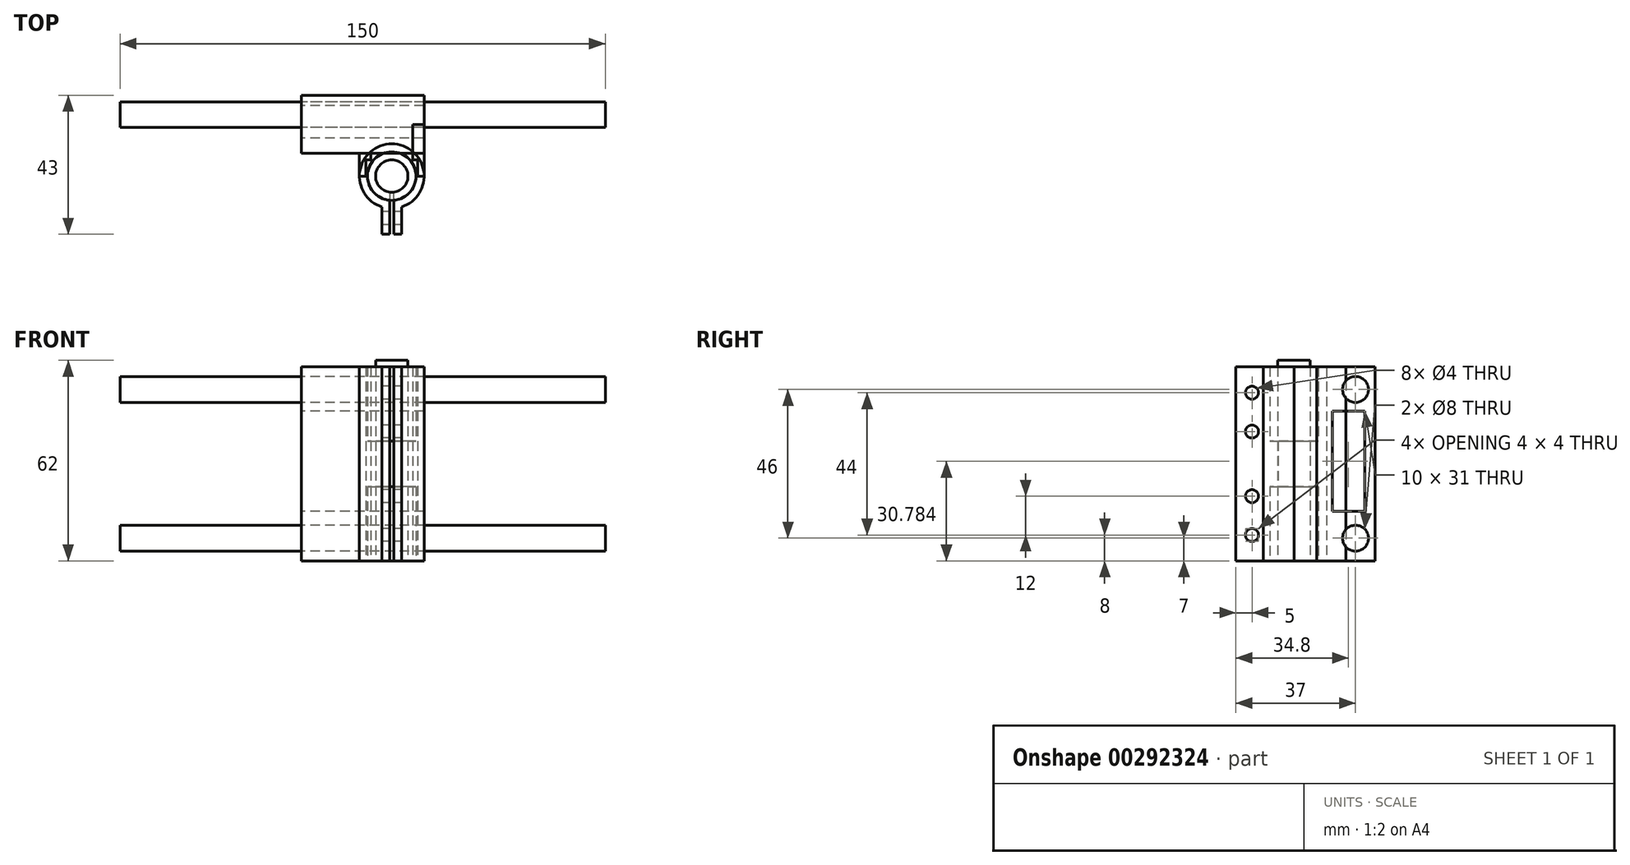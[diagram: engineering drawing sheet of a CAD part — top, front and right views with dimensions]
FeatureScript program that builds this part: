
annotation { "Feature Type Name" : "Feature", "Feature Type Description" : "" }
export const myFeature = defineFeature(function(context is Context, id is Id, definition is map)
    precondition{}
    {
        {
            var Q0;
            Q0=qCreatedBy(makeId("Top.planeOp"),FACE);
            var sketch = newSketch(context, id + "F0", { "sketchPlane" : qUnion([Q0])});
            skLineSegment(sketch, "E0.bottom", {"start": v(19, -9) * mm, "end": v(-19, -9) * mm});
            skLineSegment(sketch, "E0.top", {"start": v(19, 9) * mm, "end": v(-19, 9) * mm});
            skLineSegment(sketch, "E0.left", {"start": v(19, -9) * mm, "end": v(19, 9) * mm});
            skLineSegment(sketch, "E0.right", {"start": v(-19, -9) * mm, "end": v(-19, 9) * mm});
            skPoint(sketch, "E0.middle", {"position": v(0, 0) * mm});
            skSolve(sketch);
        }
        {
            var Q0;
            Q0=qSketchRegion(id+"F0",true);
            extrude(context, id + "F1", {"entities" : qUnion([Q0]), "depth" : 60 * mm});
        }
        {
            var Q0;
            Q0=qCreatedBy(makeId("Right.planeOp"),FACE);
            var sketch = newSketch(context, id + "F2", { "sketchPlane" : qUnion([Q0])});
            skCircle(sketch, "E1", {"center": v(0, 0) * mm, "radius": 4 * mm});
            skSolve(sketch);
        }
        {
            var Q0;
            Q0=qSketchRegion(id+"F2",true);
            extrude(context, id + "F3", {"entities" : qUnion([Q0]), "endBound" : BoundingType.SYMMETRIC, "depth" : 150 * mm});
        }
        {
            var Q0;
            Q0=makeQuery(id+"F3.opExtrude","SWEPT_BODY",BODY,{"disambiguationData":[OSD([sQuery(id+"F2.wireOp",EDGE,"E1")])]});
            transform(context, id + "F4", {"entities" : qUnion([Q0]), "transformType" : TransformType.TRANSLATION_3D, "dx" : 0 * mm, "dy" : 3 * mm, "dz" : 7 * mm, "makeCopy" : false});
        }
        {
            var Q0;
            Q0=makeQuery(id+"F3.opExtrude","SWEPT_BODY",BODY,{"disambiguationData":[OSD([sQuery(id+"F2.wireOp",EDGE,"E1")])]});
            transform(context, id + "F5", {"entities" : qUnion([Q0]), "transformType" : TransformType.COPY});
        }
        {
            var Q0;
            Q0=makeQuery(id+"F5.opPattern","COPY",BODY,{"derivedFrom":makeQuery(id+"F3.opExtrude","SWEPT_BODY",BODY,{"disambiguationData":[OSD([sQuery(id+"F2.wireOp",EDGE,"E1")])]}),"instanceName":"1"});
            transform(context, id + "F6", {"entities" : qUnion([Q0]), "transformType" : TransformType.TRANSLATION_3D, "dx" : 0 * mm, "dy" : 0 * mm, "dz" : 46 * mm, "makeCopy" : false});
        }
        {
            var Q0;
            Q0=makeQuery(id+"F3.opExtrude","SWEPT_BODY",BODY,{"disambiguationData":[OSD([sQuery(id+"F2.wireOp",EDGE,"E1")])]});
            var Q1;
            Q1=makeQuery(id+"F5.opPattern","COPY",BODY,{"derivedFrom":makeQuery(id+"F3.opExtrude","SWEPT_BODY",BODY,{"disambiguationData":[OSD([sQuery(id+"F2.wireOp",EDGE,"E1")])]}),"instanceName":"1"});
            transform(context, id + "F7", {"entities" : qUnion([Q0, Q1]), "transformType" : TransformType.COPY});
        }
        {
            var Q0;
            Q0=makeQuery(id+"F7.opPattern","COPY",BODY,{"derivedFrom":makeQuery(id+"F3.opExtrude","SWEPT_BODY",BODY,{"disambiguationData":[OSD([sQuery(id+"F2.wireOp",EDGE,"E1")])]}),"instanceName":"1"});
            var Q1;
            Q1=makeQuery(id+"F7.opPattern","COPY",BODY,{"derivedFrom":makeQuery(id+"F5.opPattern","COPY",BODY,{"derivedFrom":makeQuery(id+"F3.opExtrude","SWEPT_BODY",BODY,{"disambiguationData":[OSD([sQuery(id+"F2.wireOp",EDGE,"E1")])]}),"instanceName":"1"}),"instanceName":"1"});
            var Q2;
            Q2=makeQuery(id+"F1.opExtrude","SWEPT_BODY",BODY,{"disambiguationData":[OSD([sQuery(id+"F0.wireOp",EDGE,"E0.bottom"),sQuery(id+"F0.wireOp",EDGE,"E0.top"),sQuery(id+"F0.wireOp",EDGE,"E0.left"),sQuery(id+"F0.wireOp",EDGE,"E0.right")])]});
            booleanBodies(context, id + "F8", {"operationType" : BooleanOperationType.SUBTRACTION, "tools" : qUnion([Q0, Q1]), "targets" : qUnion([Q2])});
        }
        {
            var Q0;
            Q0=qCreatedBy(makeId("Right.planeOp"),FACE);
            var sketch = newSketch(context, id + "F9", { "sketchPlane" : qUnion([Q0])});
            skLineSegment(sketch, "E2", {"start": v(5.8, 0) * mm, "end": v(9, 0) * mm});
            skLineSegment(sketch, "E3", {"start": v(9, 0) * mm, "end": v(5.8, 0) * mm});
            skLineSegment(sketch, "E4", {"start": v(5.8, 15.28) * mm, "end": v(5.8, 46.28) * mm});
            skLineSegment(sketch, "E5", {"start": v(5.8, 15.28) * mm, "end": v(-4.2, 15.28) * mm});
            skLineSegment(sketch, "E6", {"start": v(-4.2, 15.28) * mm, "end": v(-4.2, 46.28) * mm});
            skLineSegment(sketch, "E7", {"start": v(-4.2, 46.28) * mm, "end": v(5.8, 46.28) * mm});
            skSolve(sketch);
        }
        {
            var Q0;
            Q0=qSketchRegion(id+"F9",true);
            extrude(context, id + "F10", {"entities" : qUnion([Q0]), "endBound" : BoundingType.SYMMETRIC, "depth" : 50 * mm});
        }
        {
            var Q0;
            Q0=makeQuery(id+"F10.opExtrude","SWEPT_BODY",BODY,{"disambiguationData":[OSD([sQuery(id+"F9.wireOp",EDGE,"E4"),sQuery(id+"F9.wireOp",EDGE,"E5"),sQuery(id+"F9.wireOp",EDGE,"E6"),sQuery(id+"F9.wireOp",EDGE,"E7")])]});
            var Q1;
            Q1=makeQuery(id+"F1.opExtrude","SWEPT_BODY",BODY,{"disambiguationData":[OSD([sQuery(id+"F0.wireOp",EDGE,"E0.bottom"),sQuery(id+"F0.wireOp",EDGE,"E0.top"),sQuery(id+"F0.wireOp",EDGE,"E0.left"),sQuery(id+"F0.wireOp",EDGE,"E0.right")])]});
            booleanBodies(context, id + "F11", {"operationType" : BooleanOperationType.SUBTRACTION, "tools" : qUnion([Q0]), "targets" : qUnion([Q1])});
        }
        {
            var Q0;
            Q0=qCreatedBy(makeId("Top.planeOp"),FACE);
            var sketch = newSketch(context, id + "F12", { "sketchPlane" : qUnion([Q0])});
            skCircle(sketch, "E8", {"center": v(0, 0) * mm, "radius": 7.5 * mm});
            skSolve(sketch);
        }
        {
            var Q0;
            Q0=qSketchRegion(id+"F12",true);
            extrude(context, id + "F13", {"entities" : qUnion([Q0]), "depth" : 23 * mm});
        }
        {
            var Q0;
            Q0=makeQuery(id+"F13.opExtrude","SWEPT_BODY",BODY,{"disambiguationData":[OSD([sQuery(id+"F12.wireOp",EDGE,"E8")])]});
            transform(context, id + "F14", {"entities" : qUnion([Q0]), "transformType" : TransformType.TRANSLATION_3D, "dx" : 8 * mm, "dy" : -16 * mm, "dz" : 0 * mm, "makeCopy" : false});
        }
        {
            var Q0;
            Q0=makeQuery(id+"F13.opExtrude","SWEPT_BODY",BODY,{"disambiguationData":[OSD([sQuery(id+"F12.wireOp",EDGE,"E8")])]});
            transform(context, id + "F15", {"entities" : qUnion([Q0]), "transformType" : TransformType.TRANSLATION_3D, "dx" : 0 * mm, "dy" : 2 * mm, "dz" : 0 * mm, "makeCopy" : false});
        }
        {
            var Q0;
            Q0=makeQuery(id+"F13.opExtrude","SWEPT_BODY",BODY,{"disambiguationData":[OSD([sQuery(id+"F12.wireOp",EDGE,"E8")])]});
            transform(context, id + "F16", {"entities" : qUnion([Q0]), "transformType" : TransformType.COPY});
        }
        {
            var Q0;
            Q0=makeQuery(id+"F16.opPattern","COPY",BODY,{"derivedFrom":makeQuery(id+"F13.opExtrude","SWEPT_BODY",BODY,{"disambiguationData":[OSD([sQuery(id+"F12.wireOp",EDGE,"E8")])]}),"instanceName":"1"});
            transform(context, id + "F17", {"entities" : qUnion([Q0]), "transformType" : TransformType.TRANSLATION_3D, "dx" : 0 * mm, "dy" : 0 * mm, "dz" : 37 * mm, "makeCopy" : false});
        }
        {
            var Q0;
            Q0=qCreatedBy(makeId("Top.planeOp"),FACE);
            var sketch = newSketch(context, id + "F18", { "sketchPlane" : qUnion([Q0])});
            skCircle(sketch, "E9", {"center": v(0, 0) * mm, "radius": 5 * mm});
            skSolve(sketch);
        }
        {
            var Q0;
            Q0=qSketchRegion(id+"F18",true);
            extrude(context, id + "F19", {"entities" : qUnion([Q0]), "depth" : 62 * mm});
        }
        {
            var Q0;
            Q0=makeQuery(id+"F19.opExtrude","SWEPT_BODY",BODY,{"disambiguationData":[OSD([sQuery(id+"F18.wireOp",EDGE,"E9")])]});
            transform(context, id + "F20", {"entities" : qUnion([Q0]), "transformType" : TransformType.TRANSLATION_3D, "dx" : 8 * mm, "dy" : -14 * mm, "dz" : 0 * mm, "makeCopy" : false});
        }
        {
            var Q0;
            Q0=makeQuery(id+"F13.opExtrude","SWEPT_BODY",BODY,{"disambiguationData":[OSD([sQuery(id+"F12.wireOp",EDGE,"E8")])]});
            var Q1;
            Q1=makeQuery(id+"F16.opPattern","COPY",BODY,{"derivedFrom":makeQuery(id+"F13.opExtrude","SWEPT_BODY",BODY,{"disambiguationData":[OSD([sQuery(id+"F12.wireOp",EDGE,"E8")])]}),"instanceName":"1"});
            var Q2;
            Q2=makeQuery(id+"F19.opExtrude","SWEPT_BODY",BODY,{"disambiguationData":[OSD([sQuery(id+"F18.wireOp",EDGE,"E9")])]});
            transform(context, id + "F21", {"entities" : qUnion([Q0, Q1, Q2]), "transformType" : TransformType.COPY});
        }
        {
            var Q0;
            Q0=qCreatedBy(makeId("Top.planeOp"),FACE);
            var sketch = newSketch(context, id + "F22", { "sketchPlane" : qUnion([Q0])});
            skCircle(sketch, "E10", {"center": v(0, 0) * mm, "radius": 10 * mm});
            skSolve(sketch);
        }
        {
            var Q0;
            Q0=qSketchRegion(id+"F22",true);
            extrude(context, id + "F23", {"entities" : qUnion([Q0]), "depth" : 60 * mm});
        }
        {
            var Q0;
            Q0=makeQuery(id+"F23.opExtrude","SWEPT_BODY",BODY,{"disambiguationData":[OSD([sQuery(id+"F22.wireOp",EDGE,"E10")])]});
            transform(context, id + "F24", {"entities" : qUnion([Q0]), "transformType" : TransformType.TRANSLATION_3D, "dx" : 9 * mm, "dy" : -10 * mm, "dz" : 0 * mm, "makeCopy" : false});
        }
        {
            var Q0;
            Q0=makeQuery(id+"F23.opExtrude","SWEPT_BODY",BODY,{"disambiguationData":[OSD([sQuery(id+"F22.wireOp",EDGE,"E10")])]});
            transform(context, id + "F25", {"entities" : qUnion([Q0]), "transformType" : TransformType.TRANSLATION_3D, "dx" : -1 * mm, "dy" : -4 * mm, "dz" : 0 * mm, "makeCopy" : false});
        }
        {
            var Q0;
            Q0=qCreatedBy(makeId("Top.planeOp"),FACE);
            var sketch = newSketch(context, id + "F26", { "sketchPlane" : qUnion([Q0])});
            skLineSegment(sketch, "E11", {"start": v(0, 0) * mm, "end": v(8, 0) * mm});
            skLineSegment(sketch, "E12", {"start": v(8.75, -32) * mm, "end": v(11, -32) * mm});
            skLineSegment(sketch, "E13", {"start": v(11, -32) * mm, "end": v(8.75, -32) * mm});
            skLineSegment(sketch, "E14", {"start": v(5, -32) * mm, "end": v(5, -23) * mm});
            skLineSegment(sketch, "E15", {"start": v(11, -23) * mm, "end": v(11, -32) * mm});
            skLineSegment(sketch, "E16.trimOffspring", {"start": v(8.75, -23) * mm, "end": v(11, -23) * mm});
            skLineSegment(sketch, "E17.trimOffspring", {"start": v(7.25, -32) * mm, "end": v(5, -32) * mm});
            skLineSegment(sketch, "E18", {"start": v(5, -23) * mm, "end": v(7.25, -23) * mm});
            skLineSegment(sketch, "E19", {"start": v(7.25, -32) * mm, "end": v(8.75, -32) * mm});
            skLineSegment(sketch, "E20", {"start": v(7.25, -23) * mm, "end": v(8.75, -23) * mm});
            skSolve(sketch);
        }
        {
            var Q0;
            Q0 = qSketchRegion(id + "F26", true);
            extrude(context, id + "F27", {"entities" : qUnion([Q0]), "operationType" : NewBodyOperationType.ADD, "depth" : 60 * mm});
        }
        {
            var Q0;
            Q0=qCreatedBy(makeId("Top.planeOp"),FACE);
            var sketch = newSketch(context, id + "F28", { "sketchPlane" : qUnion([Q0])});
            skLineSegment(sketch, "E21", {"start": v(0, 0) * mm, "end": v(8, 0) * mm});
            skLineSegment(sketch, "E22", {"start": v(8, -36.82) * mm, "end": v(8.6, -36.82) * mm});
            skLineSegment(sketch, "E23", {"start": v(8.6, -36.82) * mm, "end": v(8.6, -16.82) * mm});
            skLineSegment(sketch, "E24", {"start": v(8.6, -16.82) * mm, "end": v(7.4, -16.82) * mm});
            skLineSegment(sketch, "E25", {"start": v(7.4, -16.82) * mm, "end": v(7.4, -36.82) * mm});
            skLineSegment(sketch, "E26", {"start": v(7.4, -36.82) * mm, "end": v(8, -36.82) * mm});
            skSolve(sketch);
        }
        {
            var Q0;
            Q0 = qSketchRegion(id + "F28", true);
            extrude(context, id + "F29", {"entities" : qUnion([Q0]), "depth" : 60 * mm});
        }
        {
            var Q0;
            Q0=makeQuery(id+"F29.opExtrude","SWEPT_BODY",BODY,{"disambiguationData":[OSD([sQuery(id+"F28.wireOp",EDGE,"E22"),sQuery(id+"F28.wireOp",EDGE,"E23"),sQuery(id+"F28.wireOp",EDGE,"E24"),sQuery(id+"F28.wireOp",EDGE,"E25"),sQuery(id+"F28.wireOp",EDGE,"E26")])]});
            var Q1;
            Q1=makeQuery(id+"F23.opExtrude","SWEPT_BODY",BODY,{"disambiguationData":[OSD([sQuery(id+"F22.wireOp",EDGE,"E10")])]});
            booleanBodies(context, id + "F30", {"operationType" : BooleanOperationType.SUBTRACTION, "tools" : qUnion([Q0]), "targets" : qUnion([Q1])});
        }
        {
            var Q0;
            Q0=makeQuery(id+"F21.opPattern","COPY",BODY,{"derivedFrom":makeQuery(id+"F13.opExtrude","SWEPT_BODY",BODY,{"disambiguationData":[OSD([sQuery(id+"F12.wireOp",EDGE,"E8")])]}),"instanceName":"1"});
            var Q1;
            Q1=makeQuery(id+"F23.opExtrude","SWEPT_BODY",BODY,{"disambiguationData":[OSD([sQuery(id+"F22.wireOp",EDGE,"E10")])]});
            booleanBodies(context, id + "F31", {"operationType" : BooleanOperationType.SUBTRACTION, "tools" : qUnion([Q0]), "targets" : qUnion([Q1])});
        }
        {
            var Q0;
            Q0=makeQuery(id+"F21.opPattern","COPY",BODY,{"derivedFrom":makeQuery(id+"F16.opPattern","COPY",BODY,{"derivedFrom":makeQuery(id+"F13.opExtrude","SWEPT_BODY",BODY,{"disambiguationData":[OSD([sQuery(id+"F12.wireOp",EDGE,"E8")])]}),"instanceName":"1"}),"instanceName":"1"});
            var Q1;
            Q1=makeQuery(id+"F23.opExtrude","SWEPT_BODY",BODY,{"disambiguationData":[OSD([sQuery(id+"F22.wireOp",EDGE,"E10")])]});
            booleanBodies(context, id + "F32", {"operationType" : BooleanOperationType.SUBTRACTION, "tools" : qUnion([Q0]), "targets" : qUnion([Q1])});
        }
        {
            var Q0;
            Q0=makeQuery(id+"F21.opPattern","COPY",BODY,{"derivedFrom":makeQuery(id+"F19.opExtrude","SWEPT_BODY",BODY,{"disambiguationData":[OSD([sQuery(id+"F18.wireOp",EDGE,"E9")])]}),"instanceName":"1"});
            var Q1;
            Q1=makeQuery(id+"F23.opExtrude","SWEPT_BODY",BODY,{"disambiguationData":[OSD([sQuery(id+"F22.wireOp",EDGE,"E10")])]});
            booleanBodies(context, id + "F33", {"operationType" : BooleanOperationType.SUBTRACTION, "tools" : qUnion([Q0]), "targets" : qUnion([Q1])});
        }
        {
            var Q0;
            Q0=makeQuery(id+"F23.opExtrude","SWEPT_BODY",BODY,{"disambiguationData":[OSD([sQuery(id+"F22.wireOp",EDGE,"E10")])]});
            var Q1;
            Q1=makeQuery(id+"F19.opExtrude","SWEPT_BODY",BODY,{"disambiguationData":[OSD([sQuery(id+"F18.wireOp",EDGE,"E9")])]});
            var Q2;
            Q2=makeQuery(id+"F16.opPattern","COPY",BODY,{"derivedFrom":makeQuery(id+"F13.opExtrude","SWEPT_BODY",BODY,{"disambiguationData":[OSD([sQuery(id+"F12.wireOp",EDGE,"E8")])]}),"instanceName":"1"});
            var Q3;
            Q3=makeQuery(id+"F13.opExtrude","SWEPT_BODY",BODY,{"disambiguationData":[OSD([sQuery(id+"F12.wireOp",EDGE,"E8")])]});
            transform(context, id + "F34", {"entities" : qUnion([Q0, Q1, Q2, Q3]), "transformType" : TransformType.TRANSLATION_3D, "dx" : 1 * mm, "dy" : -2 * mm, "dz" : 0 * mm, "makeCopy" : false});
        }
        {
            var Q0;
            Q0=qCreatedBy(makeId("Top.planeOp"),FACE);
            var sketch = newSketch(context, id + "F35", { "sketchPlane" : qUnion([Q0])});
            skLineSegment(sketch, "E27", {"start": v(15.5, 0) * mm, "end": v(19, 0) * mm});
            skLineSegment(sketch, "E28", {"start": v(19, 0) * mm, "end": v(19, -16) * mm});
            skLineSegment(sketch, "E29", {"start": v(19, -16) * mm, "end": v(17, -16) * mm});
            skLineSegment(sketch, "E30", {"start": v(17, -16) * mm, "end": v(17, -11) * mm});
            skLineSegment(sketch, "E31", {"start": v(17, -11) * mm, "end": v(15.5, -11) * mm});
            skLineSegment(sketch, "E32", {"start": v(15.5, -11) * mm, "end": v(15.5, 0) * mm});
            skSolve(sketch);
        }
        {
            var Q0;
            Q0 = qSketchRegion(id + "F35", true);
            extrude(context, id + "F36", {"entities" : qUnion([Q0]), "depth" : 60 * mm});
        }
        {
            var Q0;
            Q0=qCreatedBy(makeId("Top.planeOp"),FACE);
            var sketch = newSketch(context, id + "F37", { "sketchPlane" : qUnion([Q0])});
            skLineSegment(sketch, "E33", {"start": v(0, 0) * mm, "end": v(0, -16) * mm});
            skLineSegment(sketch, "E34", {"start": v(0, -16) * mm, "end": v(-1, -16) * mm});
            skLineSegment(sketch, "E35", {"start": v(-1, -16) * mm, "end": v(-1, -9) * mm});
            skLineSegment(sketch, "E36", {"start": v(-1, -9) * mm, "end": v(2.5, -9) * mm});
            skLineSegment(sketch, "E37", {"start": v(2.5, -9) * mm, "end": v(2.5, -11) * mm});
            skLineSegment(sketch, "E38", {"start": v(2.5, -11) * mm, "end": v(1, -11) * mm});
            skLineSegment(sketch, "E39", {"start": v(1, -11) * mm, "end": v(1, -16) * mm});
            skLineSegment(sketch, "E40", {"start": v(1, -16) * mm, "end": v(0, -16) * mm});
            skSolve(sketch);
        }
        {
            var Q0;
            Q0 = qSketchRegion(id + "F37", true);
            extrude(context, id + "F38", {"entities" : qUnion([Q0]), "depth" : 60 * mm});
        }
        {
            var Q0;
            Q0=qCreatedBy(makeId("Right.planeOp"),FACE);
            var sketch = newSketch(context, id + "F39", { "sketchPlane" : qUnion([Q0])});
            skLineSegment(sketch, "E41", {"start": v(0, 0) * mm, "end": v(0, 10) * mm});
            skLineSegment(sketch, "E42", {"start": v(0, 10) * mm, "end": v(-29, 10) * mm});
            skCircle(sketch, "E43", {"center": v(-29, 10) * mm, "radius": 2 * mm});
            skSolve(sketch);
        }
        {
            var Q0;
            Q0 = qSketchRegion(id + "F39", true);
            extrude(context, id + "F40", {"entities" : qUnion([Q0]), "depth" : 25 * mm});
        }
        {
            var Q0;
            Q0=makeQuery(id+"F40.opExtrude","SWEPT_BODY",BODY,{"disambiguationData":[OSD([sQuery(id+"F39.wireOp",EDGE,"E43")])]});
            transform(context, id + "F41", {"entities" : qUnion([Q0]), "transformType" : TransformType.COPY});
        }
        {
            var Q0;
            Q0=makeQuery(id+"F40.opExtrude","SWEPT_BODY",BODY,{"disambiguationData":[OSD([sQuery(id+"F39.wireOp",EDGE,"E43")])]});
            var Q1;
            Q1=makeQuery(id+"F41.opPattern","COPY",BODY,{"derivedFrom":makeQuery(id+"F40.opExtrude","SWEPT_BODY",BODY,{"disambiguationData":[OSD([sQuery(id+"F39.wireOp",EDGE,"E43")])]}),"instanceName":"1"});
            transform(context, id + "F42", {"entities" : qUnion([Q0, Q1]), "transformType" : TransformType.COPY});
        }
        {
            var Q0;
            Q0=makeQuery(id+"F42.opPattern","COPY",BODY,{"derivedFrom":makeQuery(id+"F41.opPattern","COPY",BODY,{"derivedFrom":makeQuery(id+"F40.opExtrude","SWEPT_BODY",BODY,{"disambiguationData":[OSD([sQuery(id+"F39.wireOp",EDGE,"E43")])]}),"instanceName":"1"}),"instanceName":"1"});
            transform(context, id + "F43", {"entities" : qUnion([Q0]), "transformType" : TransformType.TRANSLATION_3D, "dx" : 0 * mm, "dy" : 0 * mm, "dz" : 40 * mm, "makeCopy" : false});
        }
        {
            var Q0;
            Q0=makeQuery(id+"F42.opPattern","COPY",BODY,{"derivedFrom":makeQuery(id+"F40.opExtrude","SWEPT_BODY",BODY,{"disambiguationData":[OSD([sQuery(id+"F39.wireOp",EDGE,"E43")])]}),"instanceName":"1"});
            transform(context, id + "F44", {"entities" : qUnion([Q0]), "transformType" : TransformType.TRANSLATION_3D, "dx" : 0 * mm, "dy" : 0 * mm, "dz" : 30 * mm, "makeCopy" : false});
        }
        {
            var Q0;
            Q0=makeQuery(id+"F41.opPattern","COPY",BODY,{"derivedFrom":makeQuery(id+"F40.opExtrude","SWEPT_BODY",BODY,{"disambiguationData":[OSD([sQuery(id+"F39.wireOp",EDGE,"E43")])]}),"instanceName":"1"});
            transform(context, id + "F45", {"entities" : qUnion([Q0]), "transformType" : TransformType.TRANSLATION_3D, "dx" : 0 * mm, "dy" : 0 * mm, "dz" : 10 * mm, "makeCopy" : false});
        }
        {
            var Q0;
            Q0=makeQuery(id+"F40.opExtrude","SWEPT_BODY",BODY,{"disambiguationData":[OSD([sQuery(id+"F39.wireOp",EDGE,"E43")])]});
            transform(context, id + "F46", {"entities" : qUnion([Q0]), "transformType" : TransformType.TRANSLATION_3D, "dx" : 0 * mm, "dy" : 0 * mm, "dz" : -2 * mm, "makeCopy" : false});
        }
        {
            var Q0;
            Q0=makeQuery(id+"F42.opPattern","COPY",BODY,{"derivedFrom":makeQuery(id+"F41.opPattern","COPY",BODY,{"derivedFrom":makeQuery(id+"F40.opExtrude","SWEPT_BODY",BODY,{"disambiguationData":[OSD([sQuery(id+"F39.wireOp",EDGE,"E43")])]}),"instanceName":"1"}),"instanceName":"1"});
            transform(context, id + "F47", {"entities" : qUnion([Q0]), "transformType" : TransformType.TRANSLATION_3D, "dx" : 0 * mm, "dy" : 0 * mm, "dz" : 2 * mm, "makeCopy" : false});
        }
        {
            var Q0;
            Q0=makeQuery(id+"F40.opExtrude","SWEPT_BODY",BODY,{"disambiguationData":[OSD([sQuery(id+"F39.wireOp",EDGE,"E43")])]});
            var Q1;
            Q1=makeQuery(id+"F41.opPattern","COPY",BODY,{"derivedFrom":makeQuery(id+"F40.opExtrude","SWEPT_BODY",BODY,{"disambiguationData":[OSD([sQuery(id+"F39.wireOp",EDGE,"E43")])]}),"instanceName":"1"});
            var Q2;
            Q2=makeQuery(id+"F42.opPattern","COPY",BODY,{"derivedFrom":makeQuery(id+"F40.opExtrude","SWEPT_BODY",BODY,{"disambiguationData":[OSD([sQuery(id+"F39.wireOp",EDGE,"E43")])]}),"instanceName":"1"});
            var Q3;
            Q3=makeQuery(id+"F42.opPattern","COPY",BODY,{"derivedFrom":makeQuery(id+"F41.opPattern","COPY",BODY,{"derivedFrom":makeQuery(id+"F40.opExtrude","SWEPT_BODY",BODY,{"disambiguationData":[OSD([sQuery(id+"F39.wireOp",EDGE,"E43")])]}),"instanceName":"1"}),"instanceName":"1"});
            var Q4;
            Q4=makeQuery(id+"F23.opExtrude","SWEPT_BODY",BODY,{"disambiguationData":[OSD([sQuery(id+"F22.wireOp",EDGE,"E10")])]});
            booleanBodies(context, id + "F48", {"operationType" : BooleanOperationType.SUBTRACTION, "tools" : qUnion([Q0, Q1, Q2, Q3]), "targets" : qUnion([Q4])});
        }
    });
